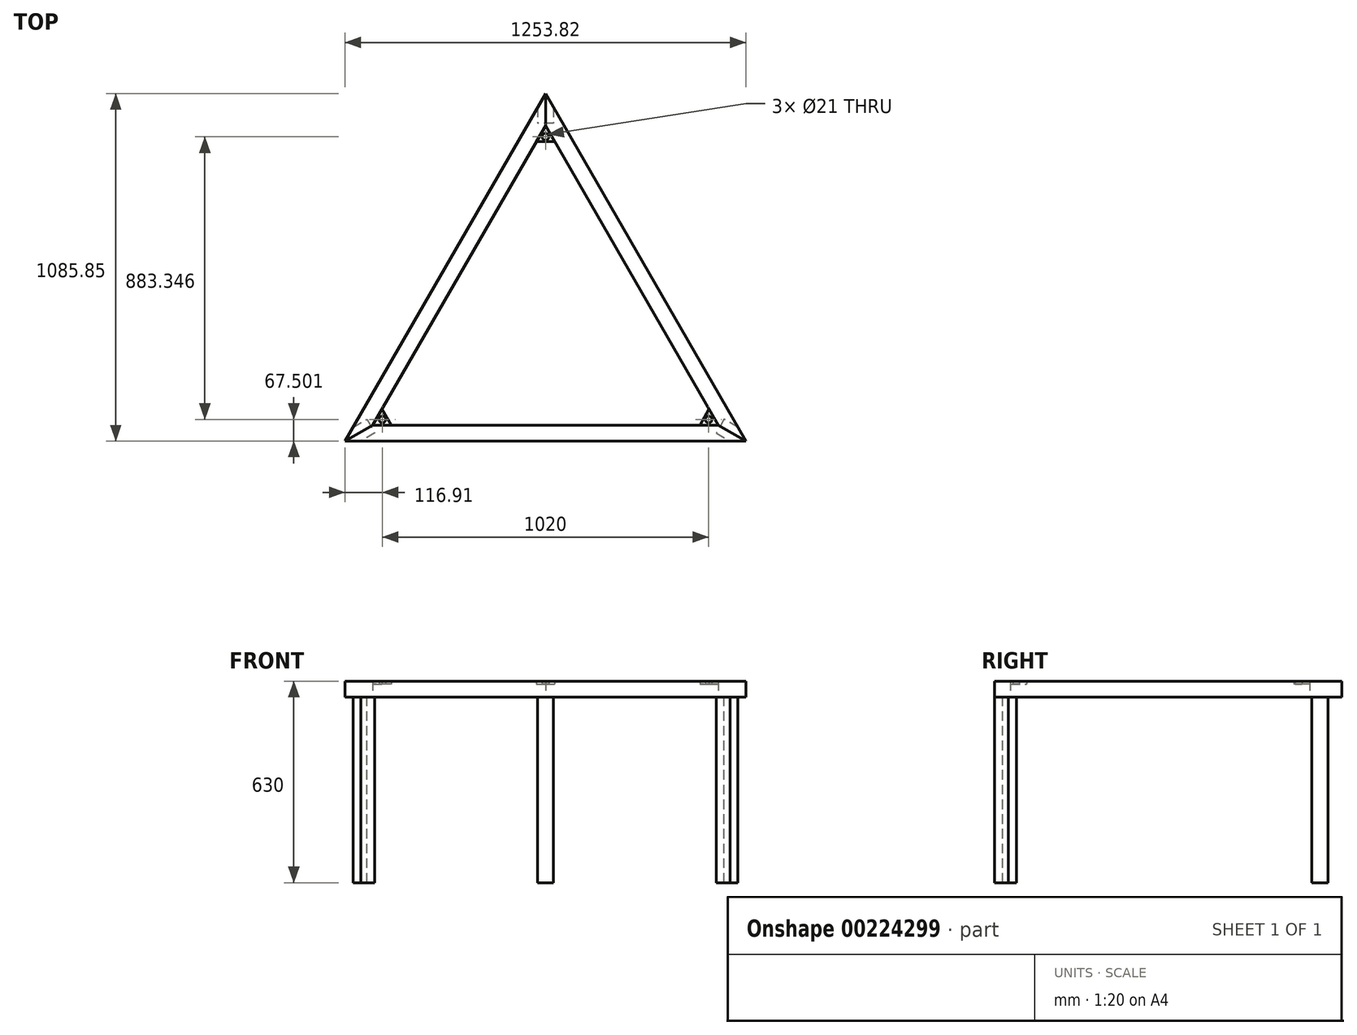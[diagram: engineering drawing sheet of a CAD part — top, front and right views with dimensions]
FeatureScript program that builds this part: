
annotation { "Feature Type Name" : "Feature", "Feature Type Description" : "" }
export const myFeature = defineFeature(function(context is Context, id is Id, definition is map)
    precondition{}
    {
        {
            var Q0;
            Q0=qCreatedBy(makeId("Top.planeOp"),FACE);
            var sketch = newSketch(context, id + "F0", { "sketchPlane" : qUnion([Q0])});
            skCircle(sketch, "E0.cCircle", {"center": v(0, 0) * mm, "radius": 311.95 * mm, "construction": true});
            skLineSegment(sketch, "E0.0", {"start": v(0, 623.9) * mm, "end": v(540.31, -311.95) * mm});
            skLineSegment(sketch, "E0.1", {"start": v(540.31, -311.95) * mm, "end": v(-540.31, -311.95) * mm});
            skLineSegment(sketch, "E0.2", {"start": v(-540.31, -311.95) * mm, "end": v(0, 623.9) * mm});
            skPoint(sketch, "E0.0.midPoint", {"position": v(270.16, 155.97) * mm});
            skLineSegment(sketch, "E1.0", {"start": v(0, 723.9) * mm, "end": v(626.91, -361.95) * mm});
            skLineSegment(sketch, "E1.1", {"start": v(-626.91, -361.95) * mm, "end": v(0, 723.9) * mm});
            skLineSegment(sketch, "E1.2", {"start": v(626.91, -361.95) * mm, "end": v(-626.91, -361.95) * mm});
            skLineSegment(sketch, "E2", {"start": v(0, 723.9) * mm, "end": v(0, 623.9) * mm});
            skLineSegment(sketch, "E3", {"start": v(-626.91, -361.95) * mm, "end": v(-540.31, -311.95) * mm});
            skLineSegment(sketch, "E4", {"start": v(540.31, -311.95) * mm, "end": v(626.91, -361.95) * mm});
            skLineSegment(sketch, "E5", {"start": v(0, 623.9) * mm, "end": v(0, 573.9) * mm});
            skLineSegment(sketch, "E6", {"start": v(-28.87, 573.9) * mm, "end": v(28.87, 573.9) * mm});
            skLineSegment(sketch, "E7", {"start": v(-540.31, -311.95) * mm, "end": v(0, 0) * mm, "construction": true});
            skLineSegment(sketch, "E8", {"start": v(0, 0) * mm, "end": v(540.31, -311.95) * mm, "construction": true});
            skLineSegment(sketch, "E9", {"start": v(-540.31, -311.95) * mm, "end": v(-497, -286.95) * mm});
            skLineSegment(sketch, "E10", {"start": v(-497, -286.95) * mm, "end": v(-511.44, -261.95) * mm});
            skLineSegment(sketch, "E11", {"start": v(-497, -286.95) * mm, "end": v(-482.58, -311.95) * mm});
            skLineSegment(sketch, "E12", {"start": v(540.31, -311.95) * mm, "end": v(497, -286.95) * mm});
            skLineSegment(sketch, "E13", {"start": v(497, -286.95) * mm, "end": v(511.44, -261.95) * mm});
            skLineSegment(sketch, "E14", {"start": v(497, -286.95) * mm, "end": v(482.58, -311.95) * mm});
            skCircle(sketch, "E15", {"center": v(-510, -294.45) * mm, "radius": 10.5 * mm});
            skCircle(sketch, "E16", {"center": v(0, 588.9) * mm, "radius": 10.5 * mm});
            skCircle(sketch, "E17", {"center": v(510, -294.45) * mm, "radius": 10.5 * mm});
            skLineSegment(sketch, "E18.bottom", {"start": v(25, 680.6) * mm, "end": v(-25, 680.6) * mm});
            skLineSegment(sketch, "E18.top", {"start": v(25, 630.6) * mm, "end": v(-25, 630.6) * mm});
            skLineSegment(sketch, "E18.left", {"start": v(25, 680.6) * mm, "end": v(25, 630.6) * mm});
            skLineSegment(sketch, "E18.right", {"start": v(-25, 680.6) * mm, "end": v(-25, 630.6) * mm});
            skPoint(sketch, "E18.middle", {"position": v(0, 655.6) * mm});
            skLineSegment(sketch, "E19", {"start": v(-601.91, -318.65) * mm, "end": v(-576.91, -361.95) * mm});
            skLineSegment(sketch, "E20", {"start": v(-601.91, -318.65) * mm, "end": v(-558.61, -293.65) * mm});
            skLineSegment(sketch, "E21", {"start": v(-558.61, -293.65) * mm, "end": v(-533.61, -336.95) * mm});
            skLineSegment(sketch, "E22", {"start": v(-533.61, -336.95) * mm, "end": v(-576.91, -361.95) * mm});
            skLineSegment(sketch, "E23", {"start": v(601.91, -318.65) * mm, "end": v(576.91, -361.95) * mm});
            skLineSegment(sketch, "E24", {"start": v(601.91, -318.65) * mm, "end": v(558.61, -293.65) * mm});
            skLineSegment(sketch, "E25", {"start": v(558.61, -293.65) * mm, "end": v(533.61, -336.95) * mm});
            skLineSegment(sketch, "E26", {"start": v(533.61, -336.95) * mm, "end": v(576.91, -361.95) * mm});
            skSolve(sketch);
        }
        {
            var Q0;
            Q0=makeQuery(id+"F0.imprint","IMPRINT",FACE,{"disambiguationData":[TD([[makeQuery(id+"F0.imprint","IMPRINT",EDGE,{"derivedFrom":sQuery(id+"F0.wireOp",EDGE,"E1.1")}),-1.0]])]});
            var Q1;
            {var subQ0=sQuery(id+"F0.wireOp",EDGE,"E18.right");Q1=makeQuery(id+"F0.imprint","IMPRINT",FACE,{"disambiguationData":[TD([[makeQuery(id+"F0.imprint","IMPRINT",EDGE,{"derivedFrom":subQ0}),-1.0]])]});}
            var Q2;
            {var subQ5=sQuery(id+"F0.wireOp",EDGE,"E18.right");Q2=makeQuery(id+"F0.imprint","IMPRINT",FACE,{"disambiguationData":[TD([[makeQuery(id+"F0.imprint","IMPRINT",EDGE,{"derivedFrom":subQ5}),1.0]])]});}
            var Q3;
            {var subQ5=sQuery(id+"F0.wireOp",EDGE,"E20");Q3=makeQuery(id+"F0.imprint","IMPRINT",FACE,{"disambiguationData":[TD([[makeQuery(id+"F0.imprint","IMPRINT",EDGE,{"derivedFrom":subQ5}),-1.0]])]});}
            extrude(context, id + "F1", {"entities" : qUnion([Q0, Q1, Q2, Q3]), "depth" : 50 * mm});
        }
        {
            var Q0;
            Q0=makeQuery(id+"F0.imprint","IMPRINT",FACE,{"disambiguationData":[TD([[makeQuery(id+"F0.imprint","IMPRINT",EDGE,{"derivedFrom":sQuery(id+"F0.wireOp",EDGE,"E1.0")}),-1.0]])]});
            var Q1;
            {var subQ0=sQuery(id+"F0.wireOp",EDGE,"E4");Q1=makeQuery(id+"F0.imprint","IMPRINT",FACE,{"disambiguationData":[TD([[makeQuery(id+"F0.imprint","IMPRINT",EDGE,{"derivedFrom":subQ0}),1.0]])]});}
            var Q2;
            {var subQ5=sQuery(id+"F0.wireOp",EDGE,"E18.left");Q2=makeQuery(id+"F0.imprint","IMPRINT",FACE,{"disambiguationData":[TD([[makeQuery(id+"F0.imprint","IMPRINT",EDGE,{"derivedFrom":subQ5}),-1.0]])]});}
            var Q3;
            {var subQ0=sQuery(id+"F0.wireOp",EDGE,"E18.left");Q3=makeQuery(id+"F0.imprint","IMPRINT",FACE,{"disambiguationData":[TD([[makeQuery(id+"F0.imprint","IMPRINT",EDGE,{"derivedFrom":subQ0}),1.0]])]});}
            var Q4;
            {var subQ5=sQuery(id+"F0.wireOp",EDGE,"E24");Q4=makeQuery(id+"F0.imprint","IMPRINT",FACE,{"disambiguationData":[TD([[makeQuery(id+"F0.imprint","IMPRINT",EDGE,{"derivedFrom":subQ5}),1.0]])]});}
            extrude(context, id + "F2", {"entities" : qUnion([Q0, Q1, Q2, Q3, Q4]), "depth" : 50 * mm});
        }
        {
            var Q0;
            Q0=makeQuery(id+"F0.imprint","IMPRINT",FACE,{"disambiguationData":[TD([[makeQuery(id+"F0.imprint","IMPRINT",EDGE,{"derivedFrom":sQuery(id+"F0.wireOp",EDGE,"E1.2")}),-1.0]])]});
            var Q1;
            {var subQ0=sQuery(id+"F0.wireOp",EDGE,"E4");Q1=makeQuery(id+"F0.imprint","IMPRINT",FACE,{"disambiguationData":[TD([[makeQuery(id+"F0.imprint","IMPRINT",EDGE,{"derivedFrom":subQ0}),-1.0]])]});}
            var Q2;
            {var subQ5=sQuery(id+"F0.wireOp",EDGE,"E22");Q2=makeQuery(id+"F0.imprint","IMPRINT",FACE,{"disambiguationData":[TD([[makeQuery(id+"F0.imprint","IMPRINT",EDGE,{"derivedFrom":subQ5}),-1.0]])]});}
            var Q3;
            {var subQ4=sQuery(id+"F0.wireOp",EDGE,"E22");Q3=makeQuery(id+"F0.imprint","IMPRINT",FACE,{"disambiguationData":[TD([[makeQuery(id+"F0.imprint","IMPRINT",EDGE,{"derivedFrom":subQ4}),1.0]])]});}
            var Q4;
            {var subQ5=sQuery(id+"F0.wireOp",EDGE,"E26");Q4=makeQuery(id+"F0.imprint","IMPRINT",FACE,{"disambiguationData":[TD([[makeQuery(id+"F0.imprint","IMPRINT",EDGE,{"derivedFrom":subQ5}),1.0]])]});}
            extrude(context, id + "F3", {"entities" : qUnion([Q0, Q1, Q2, Q3, Q4]), "depth" : 50 * mm});
        }
        {
            var Q0;
            {var subQ0=sQuery(id+"F0.wireOp",EDGE,"E6");var subQ1=sQuery(id+"F0.wireOp",EDGE,"E5");var subQ2=makeQuery(id+"F0.imprint","INTERSECT",VERTEX,{"derivedFrom":[subQ1,subQ0]});Q0=makeQuery(id+"F0.imprint","IMPRINT",FACE,{"disambiguationData":[TD([[makeQuery(id+"F0.imprint","IMPRINT",EDGE,{"disambiguationData":[TD([[subQ2,1.0]])],"derivedFrom":subQ1}),-1.0]])]});}
            var Q1;
            {var subQ0=sQuery(id+"F0.wireOp",EDGE,"E6");var subQ1=sQuery(id+"F0.wireOp",EDGE,"E5");var subQ2=makeQuery(id+"F0.imprint","INTERSECT",VERTEX,{"derivedFrom":[subQ1,subQ0]});Q1=makeQuery(id+"F0.imprint","IMPRINT",FACE,{"disambiguationData":[TD([[makeQuery(id+"F0.imprint","IMPRINT",EDGE,{"disambiguationData":[TD([[subQ2,1.0]])],"derivedFrom":subQ1}),1.0]])]});}
            extrude(context, id + "F4", {"entities" : qUnion([Q0, Q1]), "depth" : 50 * mm, "hasSecondDirection" : true, "secondDirectionOppositeDirection" : false, "secondDirectionDepth" : 40 * mm});
        }
        {
            var Q0;
            {var subQ0=sQuery(id+"F0.wireOp",EDGE,"E13");Q0=makeQuery(id+"F0.imprint","IMPRINT",FACE,{"disambiguationData":[TD([[makeQuery(id+"F0.imprint","IMPRINT",EDGE,{"derivedFrom":subQ0}),-1.0]])]});}
            var Q1;
            {var subQ0=sQuery(id+"F0.wireOp",EDGE,"E14");Q1=makeQuery(id+"F0.imprint","IMPRINT",FACE,{"disambiguationData":[TD([[makeQuery(id+"F0.imprint","IMPRINT",EDGE,{"derivedFrom":subQ0}),1.0]])]});}
            extrude(context, id + "F5", {"entities" : qUnion([Q0, Q1]), "depth" : 50 * mm, "hasSecondDirection" : true, "secondDirectionOppositeDirection" : false, "secondDirectionDepth" : 40 * mm});
        }
        {
            var Q0;
            {var subQ0=sQuery(id+"F0.wireOp",EDGE,"E10");Q0=makeQuery(id+"F0.imprint","IMPRINT",FACE,{"disambiguationData":[TD([[makeQuery(id+"F0.imprint","IMPRINT",EDGE,{"derivedFrom":subQ0}),1.0]])]});}
            var Q1;
            {var subQ0=sQuery(id+"F0.wireOp",EDGE,"E11");Q1=makeQuery(id+"F0.imprint","IMPRINT",FACE,{"disambiguationData":[TD([[makeQuery(id+"F0.imprint","IMPRINT",EDGE,{"derivedFrom":subQ0}),-1.0]])]});}
            extrude(context, id + "F6", {"entities" : qUnion([Q0, Q1]), "depth" : 50 * mm, "hasSecondDirection" : true, "secondDirectionOppositeDirection" : false, "secondDirectionDepth" : 40 * mm});
        }
        {
            var Q0;
            {var subQ5=sQuery(id+"F0.wireOp",EDGE,"E20");Q0=makeQuery(id+"F0.imprint","IMPRINT",FACE,{"disambiguationData":[TD([[makeQuery(id+"F0.imprint","IMPRINT",EDGE,{"derivedFrom":subQ5}),-1.0]])]});}
            var Q1;
            {var subQ5=sQuery(id+"F0.wireOp",EDGE,"E22");Q1=makeQuery(id+"F0.imprint","IMPRINT",FACE,{"disambiguationData":[TD([[makeQuery(id+"F0.imprint","IMPRINT",EDGE,{"derivedFrom":subQ5}),-1.0]])]});}
            extrude(context, id + "F7", {"entities" : qUnion([Q0, Q1]), "oppositeDirection" : true, "depth" : 580 * mm});
        }
        {
            var Q0;
            {var subQ5=sQuery(id+"F0.wireOp",EDGE,"E26");Q0=makeQuery(id+"F0.imprint","IMPRINT",FACE,{"disambiguationData":[TD([[makeQuery(id+"F0.imprint","IMPRINT",EDGE,{"derivedFrom":subQ5}),1.0]])]});}
            var Q1;
            {var subQ5=sQuery(id+"F0.wireOp",EDGE,"E24");Q1=makeQuery(id+"F0.imprint","IMPRINT",FACE,{"disambiguationData":[TD([[makeQuery(id+"F0.imprint","IMPRINT",EDGE,{"derivedFrom":subQ5}),1.0]])]});}
            extrude(context, id + "F8", {"entities" : qUnion([Q0, Q1]), "oppositeDirection" : true, "depth" : 580 * mm});
        }
        {
            var Q0;
            {var subQ5=sQuery(id+"F0.wireOp",EDGE,"E18.left");Q0=makeQuery(id+"F0.imprint","IMPRINT",FACE,{"disambiguationData":[TD([[makeQuery(id+"F0.imprint","IMPRINT",EDGE,{"derivedFrom":subQ5}),-1.0]])]});}
            var Q1;
            {var subQ5=sQuery(id+"F0.wireOp",EDGE,"E18.right");Q1=makeQuery(id+"F0.imprint","IMPRINT",FACE,{"disambiguationData":[TD([[makeQuery(id+"F0.imprint","IMPRINT",EDGE,{"derivedFrom":subQ5}),1.0]])]});}
            extrude(context, id + "F9", {"entities" : qUnion([Q0, Q1]), "oppositeDirection" : true, "depth" : 580 * mm});
        }
    });
